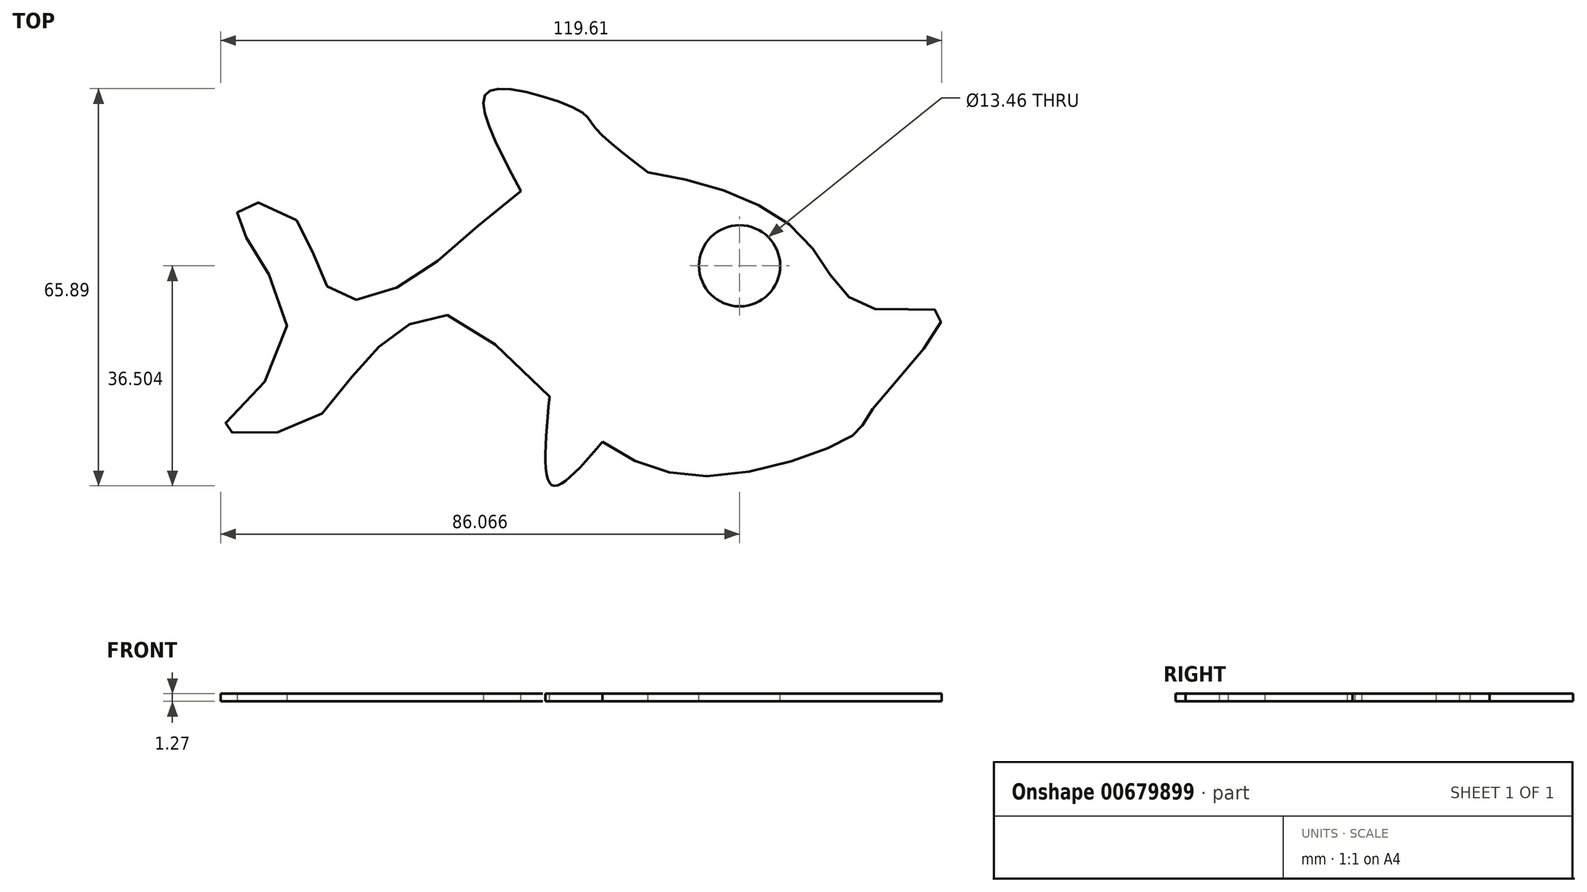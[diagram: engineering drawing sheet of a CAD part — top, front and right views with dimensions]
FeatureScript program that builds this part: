
annotation { "Feature Type Name" : "Feature", "Feature Type Description" : "" }
export const myFeature = defineFeature(function(context is Context, id is Id, definition is map)
    precondition{}
    {
        {
            var Q0;
            Q0=qCreatedBy(makeId("Top.planeOp"),FACE);
            var sketch = newSketch(context, id + "F0", { "sketchPlane" : qUnion([Q0])});
            skFitSpline(sketch, "E0", {"points": [v(25.24, 0) * mm, v(14.58, 11.68) * mm, v(-7.5, 21.74) * mm, v(-28.07, 21.44) * mm, v(-42.5, 10.63) * mm, v(-54.5, 2.52) * mm, v(-62.77, 1.92) * mm, v(-66.52, 8.53) * mm, v(-70.42, 15.28) * mm, v(-78.68, 17.09) * mm, v(-78.99, 14.38) * mm, v(-76.13, 8.83) * mm, v(-71.48, -6.8) * mm, v(-81.99, -20.3) * mm, v(-80.64, -20.76) * mm, v(-68.02, -19.56) * mm, v(-59.16, -10.1) * mm, v(-52.55, -4.09) * mm, v(-44.14, -1.39) * mm, v(-22.82, -19.1) * mm, v(0, -27.97) * mm, v(23.14, -21.06) * mm, v(25.7, -17.46) * mm, v(37.56, -1.24) * mm, v(25.24, 0) * mm]});
            skCircle(sketch, "E1", {"center": v(4.07, 6.87) * mm, "radius": 6.73 * mm});
            skFitSpline(sketch, "E2", {"points": [v(-11.12, 22.4) * mm, v(-20.14, 30.02) * mm, v(-21.97, 32.27) * mm, v(-35.73, 36.25) * mm, v(-38.4, 34.25) * mm, v(-32.22, 19.25) * mm], "startDerivative": vector(-49.52, 37.69) * mm, "endDerivative": vector(35.37, -66.8) * mm});
            skFitSpline(sketch, "E3", {"points": [v(-18.68, -22.35) * mm, v(-26.96, -29.56) * mm, v(-27.47, -14.81) * mm], "startDerivative": vector(-21.82, -25.57) * mm, "endDerivative": vector(3.6, 39.04) * mm});
            skSolve(sketch);
        }
        {
            var Q0;
            Q0=makeQuery(id+"F0.imprint","IMPRINT",FACE,{"disambiguationData":[TD([[makeQuery(id+"F0.imprint","IMPRINT",EDGE,{"derivedFrom":sQuery(id+"F0.wireOp",EDGE,"E0")}),1.0]])]});
            var Q1;
            {var subQ0=sQuery(id+"F0.wireOp",EDGE,"E2");Q1=makeQuery(id+"F0.imprint","IMPRINT",FACE,{"disambiguationData":[TD([[makeQuery(id+"F0.imprint","IMPRINT",EDGE,{"derivedFrom":subQ0}),1.0]])]});}
            var Q2;
            {var subQ0=sQuery(id+"F0.wireOp",EDGE,"E3");Q2=makeQuery(id+"F0.imprint","IMPRINT",FACE,{"disambiguationData":[TD([[makeQuery(id+"F0.imprint","IMPRINT",EDGE,{"derivedFrom":subQ0}),-1.0]])]});}
            var Q3;
            Q3=sQuery(id+"F0.wireOp",EDGE,"E0");
            var Q4;
            Q4=sQuery(id+"F0.wireOp",EDGE,"E1");
            extrude(context, id + "F1", {"entities" : qUnion([Q0, Q1, Q2]), "surfaceEntities" : qUnion([Q3, Q4]), "oppositeDirection" : true, "depth" : 1.27 * mm, "offsetDistance" : 25.4 * mm});
        }
    });
